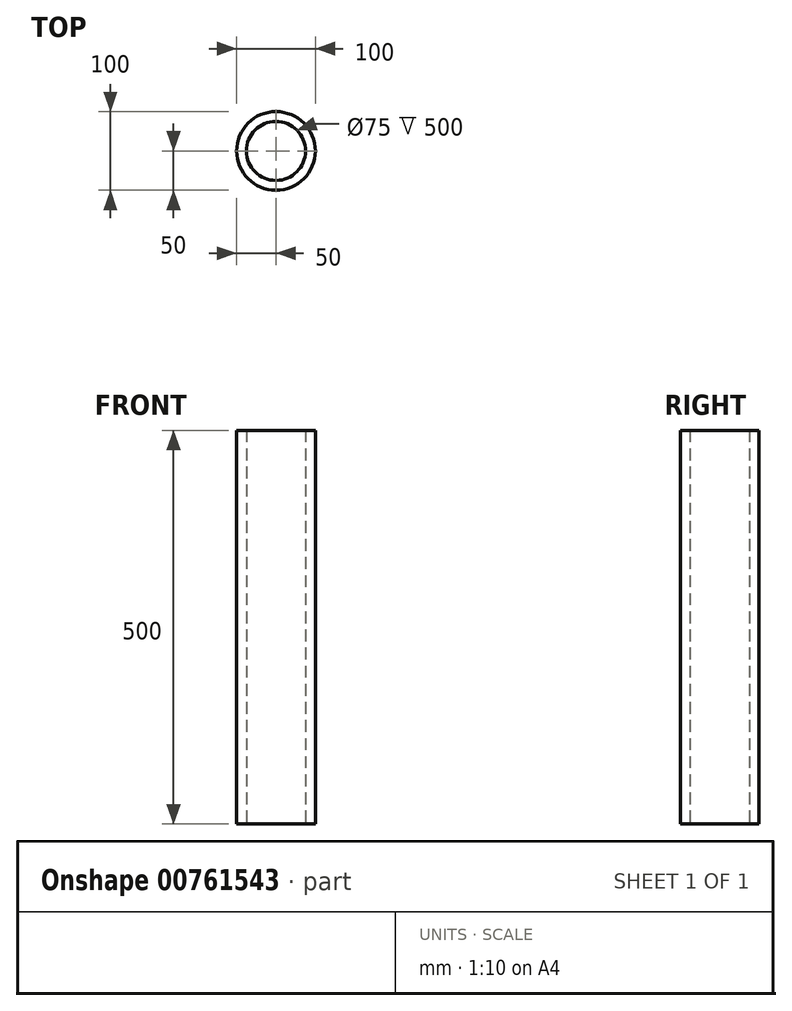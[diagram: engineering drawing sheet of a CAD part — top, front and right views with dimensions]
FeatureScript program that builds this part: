
annotation { "Feature Type Name" : "Feature", "Feature Type Description" : "" }
export const myFeature = defineFeature(function(context is Context, id is Id, definition is map)
    precondition{}
    {
        {
            var Q0;
            Q0=qCreatedBy(makeId("Top.planeOp"),FACE);
            var sketch = newSketch(context, id + "F0", { "sketchPlane" : qUnion([Q0])});
            skCircle(sketch, "E0", {"center": v(0, 0) * mm, "radius": 50 * mm});
            skCircle(sketch, "E1", {"center": v(0, 0) * mm, "radius": 37.5 * mm});
            skSolve(sketch);
        }
        {
            var Q0;
            Q0=makeQuery(id+"F0.imprint","IMPRINT",FACE,{"disambiguationData":[TD([[makeQuery(id+"F0.imprint","IMPRINT",EDGE,{"derivedFrom":sQuery(id+"F0.wireOp",EDGE,"E0")}),1.0]])]});
            extrude(context, id + "F1", {"entities" : qUnion([Q0]), "endBound" : BoundingType.SYMMETRIC, "depth" : 500 * mm, "offsetDistance" : 25 * mm});
        }
    });
